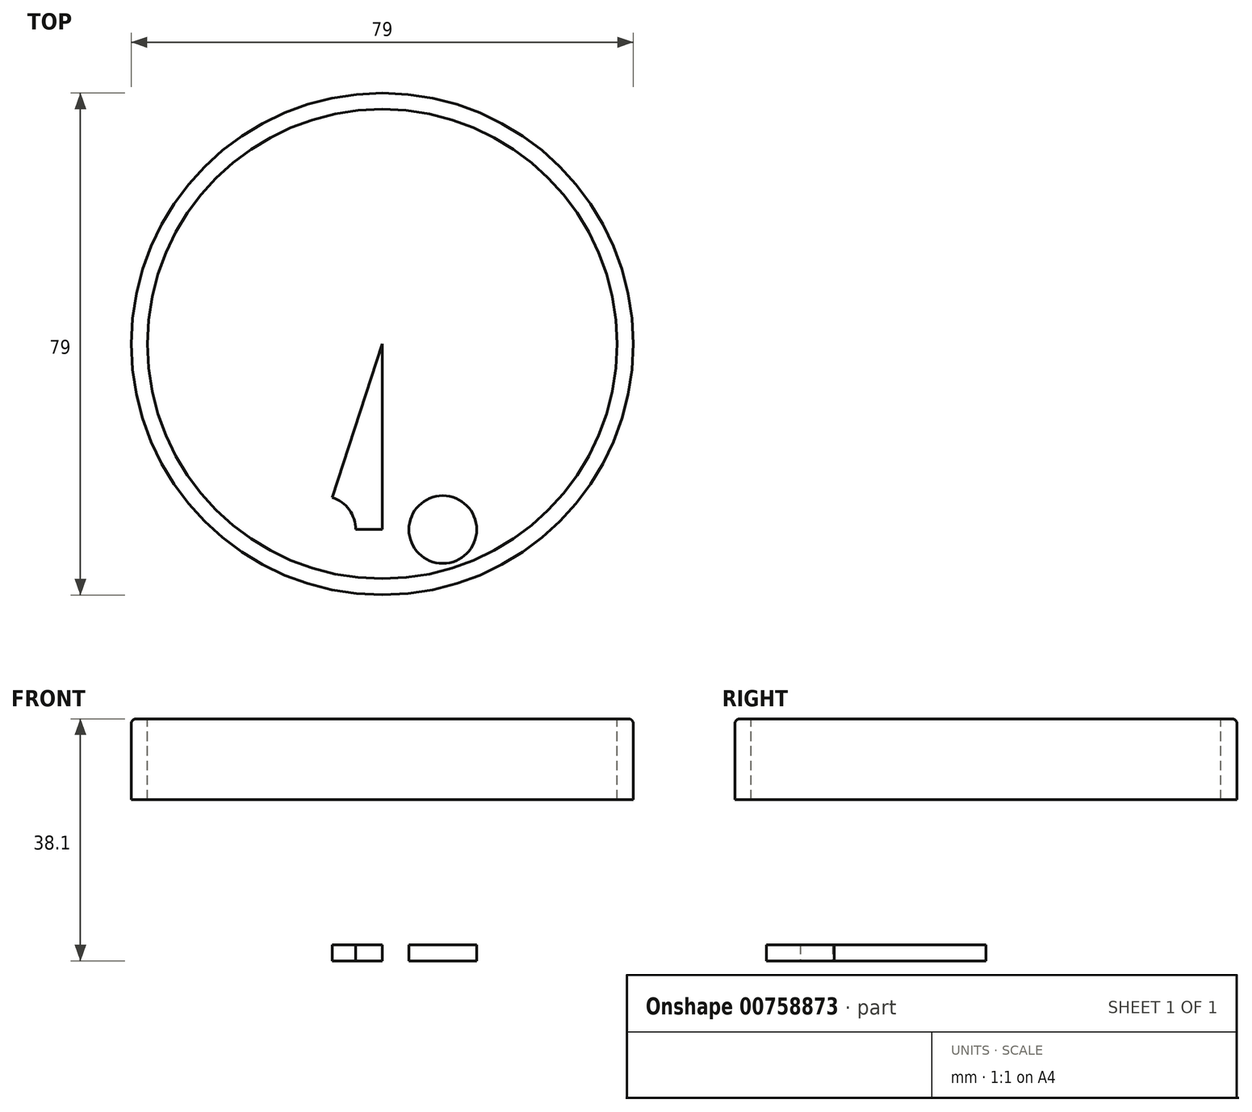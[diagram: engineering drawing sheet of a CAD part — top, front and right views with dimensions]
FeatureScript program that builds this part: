
annotation { "Feature Type Name" : "Feature", "Feature Type Description" : "" }
export const myFeature = defineFeature(function(context is Context, id is Id, definition is map)
    precondition{}
    {
        {
            var Q0;
            Q0=qCreatedBy(makeId("Top.planeOp"),FACE);
            var sketch = newSketch(context, id + "F0", { "sketchPlane" : qUnion([Q0])});
            skCircle(sketch, "E0", {"center": v(0, 0) * mm, "radius": 39.5 * mm});
            skSolve(sketch);
        }
        {
            var Q0;
            Q0=qSketchRegion(id+"F0",true);
            extrude(context, id + "F1", {"entities" : qUnion([Q0]), "depth" : 38.1 * mm, "offsetDistance" : 25.4 * mm});
        }
        {
            var Q0;
            Q0=makeQuery(id+"F1.opExtrude","CAP_FACE",FACE,{"disambiguationData":[OSD([sQuery(id+"F0.wireOp",EDGE,"E0")])],"isStart":false});
            var sketch = newSketch(context, id + "F2", { "sketchPlane" : qUnion([Q0])});
            skCircle(sketch, "E1.0", {"center": v(0, 0) * mm, "radius": 36.96 * mm});
            skSolve(sketch);
        }
        {
            var Q0;
            Q0=qSketchRegion(id+"F2",true);
            extrude(context, id + "F3", {"entities" : qUnion([Q0]), "operationType" : NewBodyOperationType.REMOVE, "oppositeDirection" : true, "depth" : 35.56 * mm, "offsetDistance" : 25.4 * mm});
        }
        {
            var Q0;
            Q0=makeQuery(id+"F3.boolean.opBoolean","COPY",EDGE,{"derivedFrom":makeQuery(id+"F3.opExtrude","CAP_EDGE",EDGE,{"disambiguationData":[OSD([sQuery(id+"F2.wireOp",EDGE,"E1.0")])],"isStart":false})});
            fillet(context, id + "F4", {"entities" : qUnion([Q0]), "radius" : 0.76 * mm, "tangentPropagation" : true, "allowEdgeOverflow" : false});
        }
        {
            var Q0;
            Q0=makeQuery(id+"F1.opExtrude","CAP_EDGE",EDGE,{"disambiguationData":[OSD([sQuery(id+"F0.wireOp",EDGE,"E0")])],"isStart":false});
            fillet(context, id + "F5", {"entities" : qUnion([Q0]), "radius" : 0.76 * mm, "tangentPropagation" : true, "allowEdgeOverflow" : false});
        }
        {
            var Q0;
            Q0=makeQuery(id+"F1.opExtrude","CAP_FACE",FACE,{"disambiguationData":[OSD([sQuery(id+"F0.wireOp",EDGE,"E0")])],"isStart":true});
            var sketch = newSketch(context, id + "F6", { "sketchPlane" : qUnion([Q0])});
            skLineSegment(sketch, "E2", {"start": v(0, 0) * mm, "end": v(0, -39.5) * mm});
            skLineSegment(sketch, "E3", {"start": v(0, -39.5) * mm, "end": v(0, -36.96) * mm});
            skLineSegment(sketch, "E4", {"start": v(0, -36.96) * mm, "end": v(0, -30.35) * mm});
            skCircle(sketch, "E5", {"center": v(0, -30.35) * mm, "radius": 5.33 * mm});
            skLineSegment(sketch, "E6", {"start": v(0, -36.96) * mm, "end": v(0, -35.69) * mm});
            skSolve(sketch);
        }
        {
            var Q0;
            Q0=qSketchRegion(id+"F6",true);
            extrude(context, id + "F7", {"entities" : qUnion([Q0]), "operationType" : NewBodyOperationType.REMOVE, "oppositeDirection" : true, "depth" : 25.4 * mm, "offsetDistance" : 25.4 * mm});
        }
        {
            var Q0;
            Q0=makeQuery(id+"F1.opExtrude","CAP_FACE",FACE,{"disambiguationData":[OSD([sQuery(id+"F0.wireOp",EDGE,"E0")])],"isStart":true});
            var sketch = newSketch(context, id + "F8", { "sketchPlane" : qUnion([Q0])});
            skLineSegment(sketch, "E7", {"start": v(0, 0) * mm, "end": v(0, 29.21) * mm});
            skLineSegment(sketch, "E8", {"start": v(0, 0) * mm, "end": v(-9.53, 29.21) * mm});
            skCircle(sketch, "E9", {"center": v(-9.53, 29.21) * mm, "radius": 5.33 * mm});
            skCircle(sketch, "E10.MirrorC", {"center": v(9.53, 29.21) * mm, "radius": 5.33 * mm});
            skLineSegment(sketch, "E11", {"start": v(-9.53, 29.2) * mm, "end": v(9.53, 29.21) * mm});
            skSolve(sketch);
        }
        {
            var Q0;
            Q0=makeQuery(id+"F8.imprint","IMPRINT",FACE,{"disambiguationData":[TD([[makeQuery(id+"F8.imprint","IMPRINT",EDGE,{"derivedFrom":sQuery(id+"F8.wireOp",EDGE,"E10.MirrorC")}),-1.0]])]});
            var Q1;
            {var subQ0=sQuery(id+"F8.wireOp",EDGE,"E11");var subQ1=sQuery(id+"F8.wireOp",EDGE,"E8");var subQ2=makeQuery(id+"F8.imprint","INTERSECT",VERTEX,{"derivedFrom":[subQ1,subQ0]});Q1=makeQuery(id+"F8.imprint","IMPRINT",FACE,{"disambiguationData":[TD([[makeQuery(id+"F8.imprint","IMPRINT",EDGE,{"disambiguationData":[TD([[subQ2,1.0]])],"derivedFrom":subQ1}),1.0]])]});}
            var Q2;
            {var subQ0=sQuery(id+"F8.wireOp",EDGE,"E11");var subQ1=sQuery(id+"F8.wireOp",EDGE,"E8");var subQ2=makeQuery(id+"F8.imprint","INTERSECT",VERTEX,{"derivedFrom":[subQ1,subQ0]});Q2=makeQuery(id+"F8.imprint","IMPRINT",FACE,{"disambiguationData":[TD([[makeQuery(id+"F8.imprint","IMPRINT",EDGE,{"disambiguationData":[TD([[subQ2,1.0]])],"derivedFrom":subQ1}),-1.0]])]});}
            extrude(context, id + "F9", {"entities" : qUnion([Q0, Q1, Q2]), "operationType" : NewBodyOperationType.REMOVE, "oppositeDirection" : true, "depth" : 25.4 * mm, "offsetDistance" : 25.4 * mm});
        }
    });
